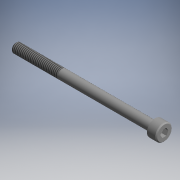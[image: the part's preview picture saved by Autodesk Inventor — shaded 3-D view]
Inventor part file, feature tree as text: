
AUTODESK INVENTOR PART (.ipt)
format: ipt  version: 2017.3 (Build 213256000, 256)  size: 117,248 bytes
history: native  units: mm (DEFAULTED — no unit token found)
features: other x14, sketch x3, revolve x1, thread x1, hole x1, extrude x1
ambient origin geometry x8: Origin, YZ Plane, XZ Plane, XY Plane, X Axis, Y Axis, Z Axis, Center Point
bodies: Solid1 (feature_tree)
feature tree (21):
  revolve  "Revolution1"  [1 undecoded]
  thread  "Thread1"  [1 undecoded]
  hole  "Hole1"  [1 undecoded]
  extrude  "Extrusion1"  [1 undecoded]
  other  "bolt_to_nut_XY"
  other  "bolt_to_nut_YZ"
  other  "bolt_to_nut_ZX"
  other  "bolt_to_nut_X"
  other  "bolt_to_nut_Y"
  other  "bolt_to_nut_Z"
  other  "bolt_to_nut_Center"
  other  "screw1_XY"
  other  "screw1_YZ"
  other  "screw1_ZX"
  other  "screw1_X"
  other  "screw1_Y"
  other  "screw1_Z"
  other  "screw1_Center"
  sketch  "Sketch_2"  dims[d0=360.0deg d1=19.5705mm d2=0.0mm]
  sketch  "Sketch2"  dims[d3=3.0mm d4=6.0mm d5=4.0mm d6=2.0mm d7=90.0deg d8=2.0mm d9=150.0deg d10=2.0mm d11=0.0mm]
  sketch  "Sketch_3"  dims[d12=0.0mm d13=0.0mm]
note: 4 required parameter values undecoded (feature->parameter linkage not recoverable at this tier; creation-order binding heuristic only, values carry confidence <= 0.55)